# Revit family: Haworth_Masters_Lateral_Open
name_source: partatom
category: Furniture Systems
revit_build: Autodesk Revit 2018 (Build: 20170223_1515(x64)
units: mm (PartAtom-declared; Revit-internal decimal feet)

## family parameters
Always vertical = Yes
Cut with Voids When Loaded = No
OmniClass Number = 23.40.70.14.64.21
OmniClass Title = Systems Furniture
Part Type = Normal
Room Calculation Point = No
Round Connector Dimension = Use Diameter
Shared = No
Work Plane-Based = No

## types (1)
- Lateral Lateral
    Actual Depth = 23"
    Actual Height = 21 1/2"
    Actual Width = 30"
    Assembly Code = E2020200
    Attached = Yes
    Back Edge Of Top = 4"
    Bar Pull = No
    Bar Pull Length = 24"
    Base Clearance = 0"
    Cabinet Finish = Haworth _ Wood _ White Oak
    Classic Pull = No
    Custom Size = No
    Depth 18 or 18.75 = No
    Depth 23 or 23.75 = Yes
    Description = Haworth - Masters - Lateral - Attached
    Drawer 1 Height = 13"
    Drawer 2 Height = 6 1/2"
    Drawer 3 Offset = 1/8"
    Drawer Finish = Haworth _ Wood _ White Oak
    Finger Pull = No
    Finished Back = Yes
    Linear Pull = Yes
    Manufacturer = Haworth
    Max Width = 42"
    Max. Depth = 23 3/4"
    Max. Height = 28"
    Min Width = 24"
    Min. Depth = 18"
    Min. Height = 15 3/16"
    Model = Haworth - Masters - Lateral - Attached
    One And A Half High = Yes
    One High = No
    Pull Finish = Haworth _ Metal _ Brushed Aluminum
    Revision Number = 3
    Size = Verify Final Dim. w/ Haworth
    Standard Depths = 18, 18.75, 23, 23.75 in
    Standard Widths = 30, 36 in
    Sustainability Info = http://www.haworth.com
    Top Drawer = Yes
    Two High = No
    URL = www.haworth.com
    URL - Product = http://www.haworth.com
    Warranty = http://www.haworth.com
    Width = 30"

## geometry (parser evidence)
native form markers: Sweep x9
no freeform markers — native parametric forms only
